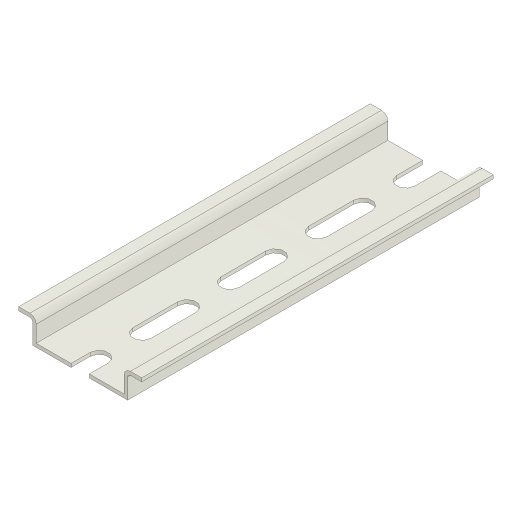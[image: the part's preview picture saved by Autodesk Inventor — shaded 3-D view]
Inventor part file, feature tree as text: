
AUTODESK INVENTOR PART (.ipt)
format: ipt  version: 2024.3 (Build 283343000, 343)  size: 271,360 bytes
history: native  units: in
note: dims shown in document units (in); Inventor stores cm internally (conversion verified against a paired STEP export)
features: extrude x1, sketch x1, imported_body x1
ambient origin geometry x8: Origin, YZ Plane, XZ Plane, XY Plane, X Axis, Y Axis, Z Axis, Center Point
bodies: Solid1 (feature_tree)
feature tree (3):
  extrude  "Extrusion1"  [1 undecoded]
  sketch  "Sketch1"  dims[d0=74.8031in d1=0.0in]
  imported_body  "Base1"
note: 1 required parameter value undecoded (feature->parameter linkage not recoverable at this tier; creation-order binding heuristic only, values carry confidence <= 0.55)
